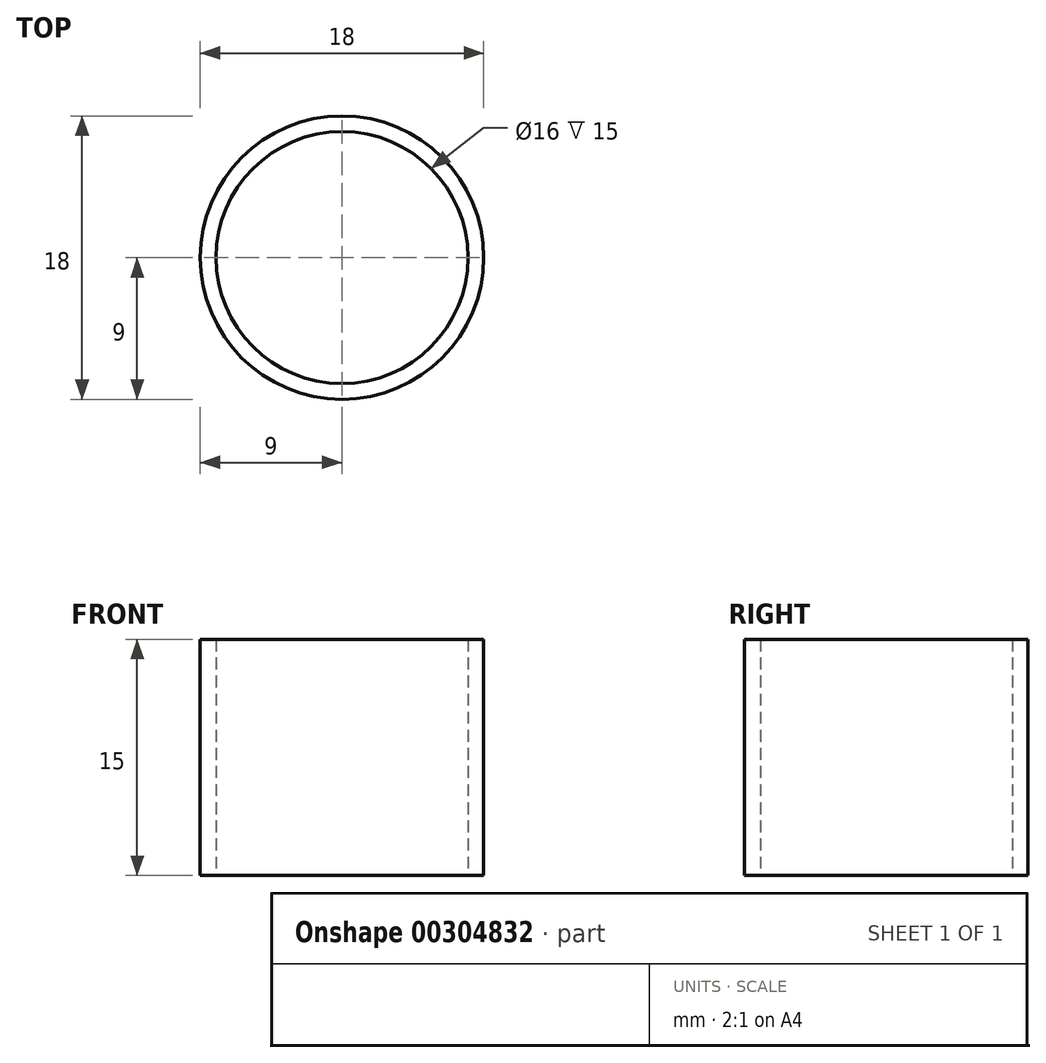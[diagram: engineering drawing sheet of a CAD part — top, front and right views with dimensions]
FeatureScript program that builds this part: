
annotation { "Feature Type Name" : "Feature", "Feature Type Description" : "" }
export const myFeature = defineFeature(function(context is Context, id is Id, definition is map)
    precondition{}
    {
        {
            var Q0;
            Q0=qCreatedBy(makeId("Top.planeOp"),FACE);
            var sketch = newSketch(context, id + "F0", { "sketchPlane" : qUnion([Q0])});
            skCircle(sketch, "E0", {"center": v(0, 0) * mm, "radius": 8 * mm});
            skCircle(sketch, "E1", {"center": v(0, 0) * mm, "radius": 9 * mm});
            skSolve(sketch);
        }
        {
            var Q0;
            Q0 = qSketchRegion(id + "F0", true);
            extrude(context, id + "F1", {"entities" : qUnion([Q0]), "depth" : 15 * mm});
        }
    });
